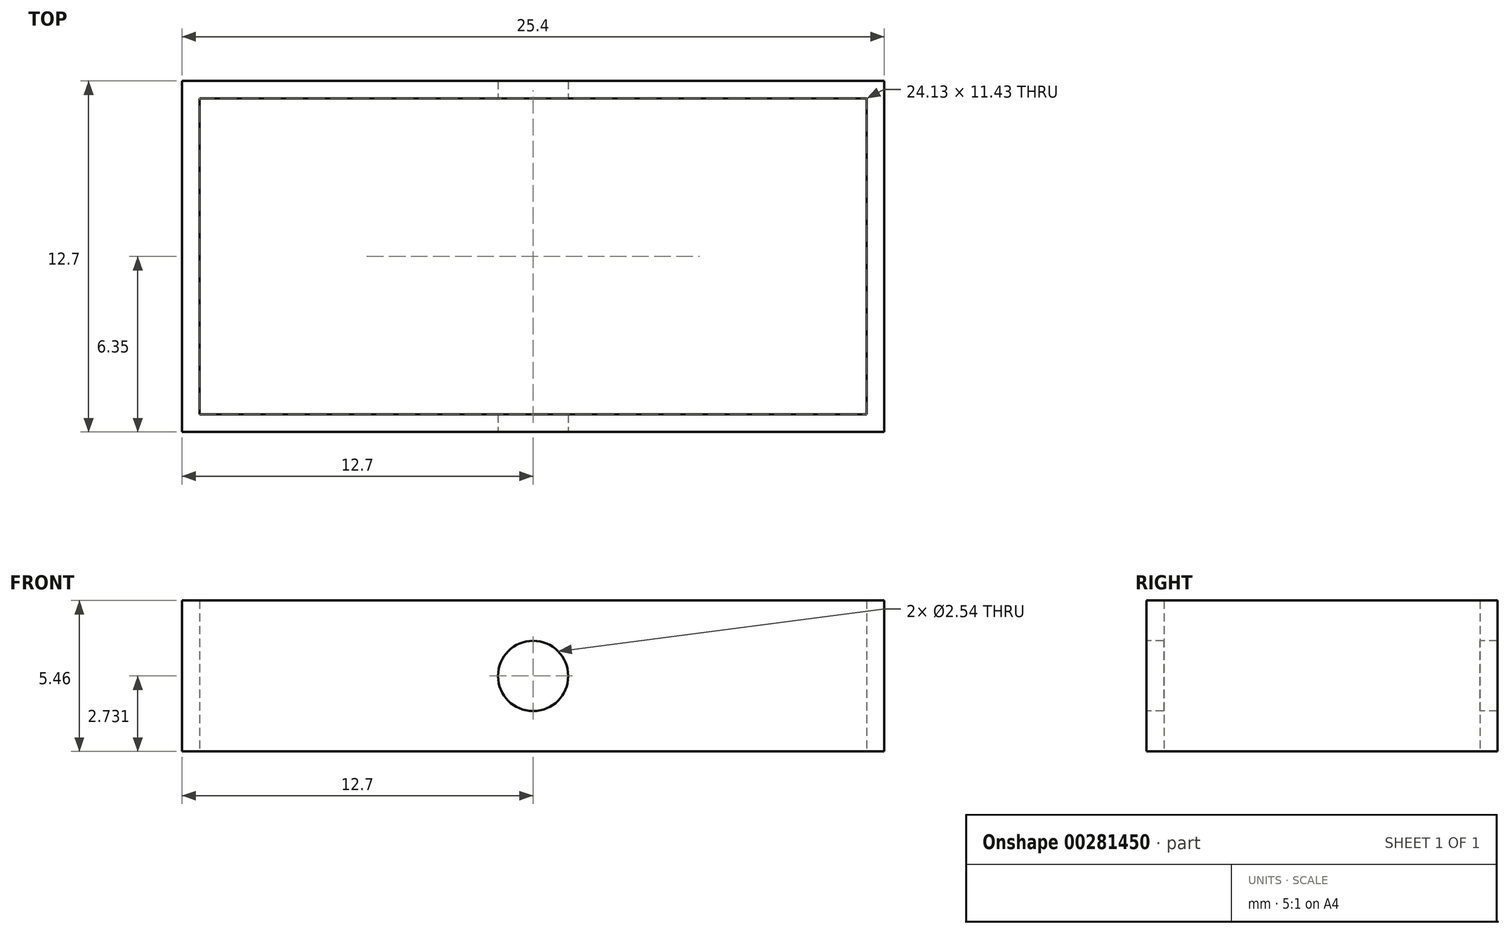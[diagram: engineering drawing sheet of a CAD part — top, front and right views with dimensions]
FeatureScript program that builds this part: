
annotation { "Feature Type Name" : "Feature", "Feature Type Description" : "" }
export const myFeature = defineFeature(function(context is Context, id is Id, definition is map)
    precondition{}
    {
        {
            var Q0;
            Q0=qCreatedBy(makeId("Top.planeOp"),FACE);
            var sketch = newSketch(context, id + "F0", { "sketchPlane" : qUnion([Q0])});
            skLineSegment(sketch, "E0.bottom", {"start": v(12.7, 6.35) * mm, "end": v(-12.7, 6.35) * mm});
            skLineSegment(sketch, "E0.top", {"start": v(12.7, -6.35) * mm, "end": v(-12.7, -6.35) * mm});
            skLineSegment(sketch, "E0.left", {"start": v(12.7, 6.35) * mm, "end": v(12.7, -6.35) * mm});
            skLineSegment(sketch, "E0.right", {"start": v(-12.7, 6.35) * mm, "end": v(-12.7, -6.35) * mm});
            skPoint(sketch, "E0.middle", {"position": v(0, 0) * mm});
            skLineSegment(sketch, "E1.bottom", {"start": v(12.07, 5.72) * mm, "end": v(-12.07, 5.72) * mm});
            skLineSegment(sketch, "E1.top", {"start": v(12.07, -5.72) * mm, "end": v(-12.07, -5.72) * mm});
            skLineSegment(sketch, "E1.left", {"start": v(12.07, 5.72) * mm, "end": v(12.07, -5.72) * mm});
            skLineSegment(sketch, "E1.right", {"start": v(-12.07, 5.72) * mm, "end": v(-12.07, -5.72) * mm});
            skSolve(sketch);
        }
        {
            var Q0;
            Q0=makeQuery(id+"F0.imprint","IMPRINT",FACE,{"disambiguationData":[TD([[makeQuery(id+"F0.imprint","IMPRINT",EDGE,{"derivedFrom":sQuery(id+"F0.wireOp",EDGE,"E0.bottom")}),1.0]])]});
            extrude(context, id + "F1", {"entities" : qUnion([Q0]), "depth" : 5.46 * mm});
        }
        {
            var Q0;
            Q0=makeQuery(id+"F1.opExtrude","SWEPT_FACE",FACE,{"disambiguationData":[OSD([sQuery(id+"F0.wireOp",EDGE,"E0.top")])]});
            var sketch = newSketch(context, id + "F2", { "sketchPlane" : qUnion([Q0])});
            skPoint(sketch, "E2", {"position": v(0, 2.73) * mm});
            skPoint(sketch, "E3.end.orphan", {"position": v(0, 0) * mm});
            skSolve(sketch);
        }
        {
            var Q0;
            Q0=sQuery(id+"F2.wireOp",VERTEX,"E2");
            var Q1;
            Q1=makeQuery(id+"F1.opExtrude","SWEPT_BODY",BODY,{"disambiguationData":[OSD([sQuery(id+"F0.wireOp",EDGE,"E0.bottom"),sQuery(id+"F0.wireOp",EDGE,"E0.top"),sQuery(id+"F0.wireOp",EDGE,"E0.left"),sQuery(id+"F0.wireOp",EDGE,"E0.right"),sQuery(id+"F0.wireOp",EDGE,"E1.bottom"),sQuery(id+"F0.wireOp",EDGE,"E1.top"),sQuery(id+"F0.wireOp",EDGE,"E1.left"),sQuery(id+"F0.wireOp",EDGE,"E1.right")])]});
            hole(context, id + "F3", {"style" : HoleStyle.SIMPLE, "endStyle" : HoleEndStyle.BLIND, "holeDiameter" : 2.54 * mm, "holeDepth" : 25.4 * mm, "tappedDepth" : 12.7 * mm, "tapClearance" : 3, "startFromSketch" : true, "locations" : qUnion([Q0]), "scope" : qUnion([Q1])});
        }
    });
